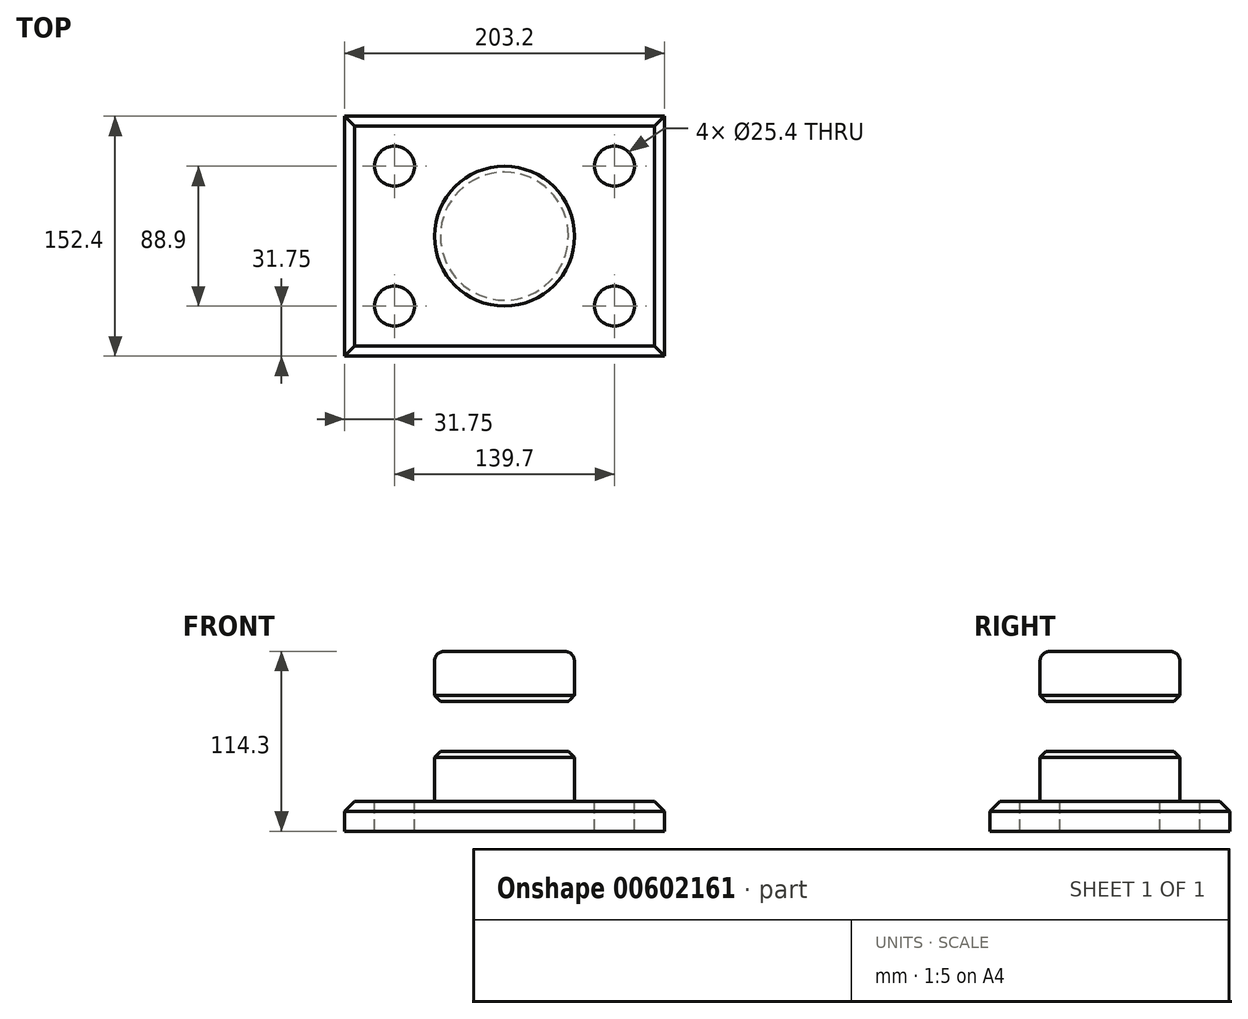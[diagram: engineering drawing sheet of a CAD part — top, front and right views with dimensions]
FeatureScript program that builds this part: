
annotation { "Feature Type Name" : "Feature", "Feature Type Description" : "" }
export const myFeature = defineFeature(function(context is Context, id is Id, definition is map)
    precondition{}
    {
        {
            var Q0;
            Q0=qCreatedBy(makeId("Top.planeOp"),FACE);
            var sketch = newSketch(context, id + "F0", { "sketchPlane" : qUnion([Q0])});
            skLineSegment(sketch, "E0.bottom", {"start": v(101.6, -76.2) * mm, "end": v(-101.6, -76.2) * mm});
            skLineSegment(sketch, "E0.top", {"start": v(101.6, 76.2) * mm, "end": v(-101.6, 76.2) * mm});
            skLineSegment(sketch, "E0.left", {"start": v(101.6, -76.2) * mm, "end": v(101.6, 76.2) * mm});
            skLineSegment(sketch, "E0.right", {"start": v(-101.6, -76.2) * mm, "end": v(-101.6, 76.2) * mm});
            skPoint(sketch, "E0.middle", {"position": v(0, 0) * mm});
            skSolve(sketch);
        }
        {
            var Q0;
            Q0=makeQuery(id+"F0.imprint","IMPRINT",FACE,{"disambiguationData":[TD([[makeQuery(id+"F0.imprint","IMPRINT",EDGE,{"derivedFrom":sQuery(id+"F0.wireOp",EDGE,"E0.bottom")}),-1.0]])]});
            extrude(context, id + "F1", {"entities" : qUnion([Q0]), "depth" : 19.05 * mm, "offsetDistance" : 25.4 * mm});
        }
        {
            var Q0;
            Q0=makeQuery(id+"F1.opExtrude","CAP_EDGE",EDGE,{"disambiguationData":[OSD([sQuery(id+"F0.wireOp",EDGE,"E0.bottom")])],"isStart":false});
            var Q1;
            Q1=makeQuery(id+"F1.opExtrude","CAP_EDGE",EDGE,{"disambiguationData":[OSD([sQuery(id+"F0.wireOp",EDGE,"E0.left")])],"isStart":false});
            var Q2;
            Q2=makeQuery(id+"F1.opExtrude","CAP_EDGE",EDGE,{"disambiguationData":[OSD([sQuery(id+"F0.wireOp",EDGE,"E0.right")])],"isStart":false});
            var Q3;
            Q3=makeQuery(id+"F1.opExtrude","CAP_EDGE",EDGE,{"disambiguationData":[OSD([sQuery(id+"F0.wireOp",EDGE,"E0.top")])],"isStart":false});
            chamfer(context, id + "F2", {"entities" : qUnion([Q0, Q1, Q2, Q3]), "width" : 6.35 * mm, "tangentPropagation" : true});
        }
        {
            var Q0;
            Q0=makeQuery(id+"F1.opExtrude","CAP_FACE",FACE,{"disambiguationData":[OSD([sQuery(id+"F0.wireOp",EDGE,"E0.bottom"),sQuery(id+"F0.wireOp",EDGE,"E0.top"),sQuery(id+"F0.wireOp",EDGE,"E0.left"),sQuery(id+"F0.wireOp",EDGE,"E0.right")])],"isStart":false});
            var sketch = newSketch(context, id + "F3", { "sketchPlane" : qUnion([Q0])});
            skPoint(sketch, "E1", {"position": v(-69.85, 44.45) * mm});
            skPoint(sketch, "E2", {"position": v(-69.85, -44.45) * mm});
            skPoint(sketch, "E3", {"position": v(69.85, -44.45) * mm});
            skPoint(sketch, "E4", {"position": v(69.85, 44.45) * mm});
            skSolve(sketch);
        }
        {
            var Q0;
            Q0=sQuery(id+"F3.wireOp",VERTEX,"E1");
            var Q1;
            Q1=sQuery(id+"F3.wireOp",VERTEX,"E4");
            var Q2;
            Q2=sQuery(id+"F3.wireOp",VERTEX,"E3");
            var Q3;
            Q3=sQuery(id+"F3.wireOp",VERTEX,"E2");
            var Q4;
            Q4=makeQuery(id+"F1.opExtrude","SWEPT_BODY",BODY,{"disambiguationData":[OSD([sQuery(id+"F0.wireOp",EDGE,"E0.bottom"),sQuery(id+"F0.wireOp",EDGE,"E0.top"),sQuery(id+"F0.wireOp",EDGE,"E0.left"),sQuery(id+"F0.wireOp",EDGE,"E0.right")])]});
            hole(context, id + "F4", {"style" : HoleStyle.SIMPLE, "endStyle" : HoleEndStyle.THROUGH, "holeDiameter" : 25.4 * mm, "majorDiameter" : 6.35 * mm, "isTappedThrough" : true, "tappedDepth" : 12.7 * mm, "tapClearance" : 3, "locations" : qUnion([Q0, Q1, Q2, Q3]), "scope" : qUnion([Q4])});
        }
        {
            var Q0;
            Q0=qCreatedBy(makeId("Front.planeOp"),FACE);
            var sketch = newSketch(context, id + "F5", { "sketchPlane" : qUnion([Q0])});
            skLineSegment(sketch, "E5.bottom", {"start": v(0, 50.8) * mm, "end": v(44.45, 50.8) * mm});
            skLineSegment(sketch, "E5.top", {"start": v(0, 19.05) * mm, "end": v(44.45, 19.05) * mm});
            skLineSegment(sketch, "E5.left", {"start": v(0, 50.8) * mm, "end": v(0, 19.05) * mm});
            skLineSegment(sketch, "E5.right", {"start": v(44.45, 50.8) * mm, "end": v(44.45, 19.05) * mm});
            skLineSegment(sketch, "E6.bottom", {"start": v(0, 50.8) * mm, "end": v(31.75, 50.8) * mm});
            skLineSegment(sketch, "E6.top", {"start": v(0, 82.55) * mm, "end": v(31.75, 82.55) * mm});
            skLineSegment(sketch, "E6.left", {"start": v(0, 50.8) * mm, "end": v(0, 82.55) * mm});
            skLineSegment(sketch, "E6.right", {"start": v(31.75, 50.8) * mm, "end": v(31.75, 82.55) * mm});
            skLineSegment(sketch, "E7.bottom", {"start": v(0, 82.55) * mm, "end": v(44.45, 82.55) * mm});
            skLineSegment(sketch, "E7.top", {"start": v(0, 114.3) * mm, "end": v(44.45, 114.3) * mm});
            skLineSegment(sketch, "E7.left", {"start": v(0, 82.55) * mm, "end": v(0, 114.3) * mm});
            skLineSegment(sketch, "E7.right", {"start": v(44.45, 82.55) * mm, "end": v(44.45, 114.3) * mm});
            skSolve(sketch);
        }
        {
            var Q0;
            Q0=makeQuery(id+"F5.imprint","IMPRINT",FACE,{"disambiguationData":[TD([[makeQuery(id+"F5.imprint","IMPRINT",EDGE,{"derivedFrom":sQuery(id+"F5.wireOp",EDGE,"E7.top")}),-1.0]])]});
            var Q1;
            Q1=makeQuery(id+"F5.imprint","IMPRINT",FACE,{"disambiguationData":[TD([[makeQuery(id+"F5.imprint","IMPRINT",EDGE,{"derivedFrom":sQuery(id+"F5.wireOp",EDGE,"E6.bottom")}),1.0]])]});
            var Q2;
            Q2=makeQuery(id+"F5.imprint","IMPRINT",FACE,{"disambiguationData":[TD([[makeQuery(id+"F5.imprint","IMPRINT",EDGE,{"derivedFrom":sQuery(id+"F5.wireOp",EDGE,"E5.bottom")}),-1.0]])]});
            var Q3;
            Q3=sQuery(id+"F5.wireOp",EDGE,"E5.left");
            revolve(context, id + "F6", {"operationType" : NewBodyOperationType.ADD, "entities" : qUnion([Q0, Q1, Q2]), "axis" : qUnion([Q3]), "revolveType" : RevolveType.FULL});
        }
        {
            var Q0;
            Q0=makeQuery(id+"F6.opRevolve","SWEPT_EDGE",EDGE,{"disambiguationData":[OSD([sQuery(id+"F5.wireOp",EDGE,"E7.top"),sQuery(id+"F5.wireOp",EDGE,"E7.right")])]});
            var Q1;
            Q1=makeQuery(id+"F6.opRevolve","SWEPT_EDGE",EDGE,{"disambiguationData":[OSD([sQuery(id+"F5.wireOp",EDGE,"E5.top"),sQuery(id+"F5.wireOp",EDGE,"E5.right")])]});
            fillet(context, id + "F7", {"entities" : qUnion([Q0, Q1]), "radius" : 6.35 * mm, "tangentPropagation" : true, "allowEdgeOverflow" : false});
        }
        {
            var Q0;
            Q0=makeQuery(id+"F6.opRevolve","SWEPT_EDGE",EDGE,{"disambiguationData":[OSD([sQuery(id+"F5.wireOp",EDGE,"E5.bottom"),sQuery(id+"F5.wireOp",EDGE,"E5.right")])]});
            var Q1;
            Q1=makeQuery(id+"F6.opRevolve","SWEPT_EDGE",EDGE,{"disambiguationData":[OSD([sQuery(id+"F5.wireOp",EDGE,"E7.bottom"),sQuery(id+"F5.wireOp",EDGE,"E7.right")])]});
            chamfer(context, id + "F8", {"entities" : qUnion([Q0, Q1]), "width" : 3.8 * mm, "tangentPropagation" : true});
        }
    });
